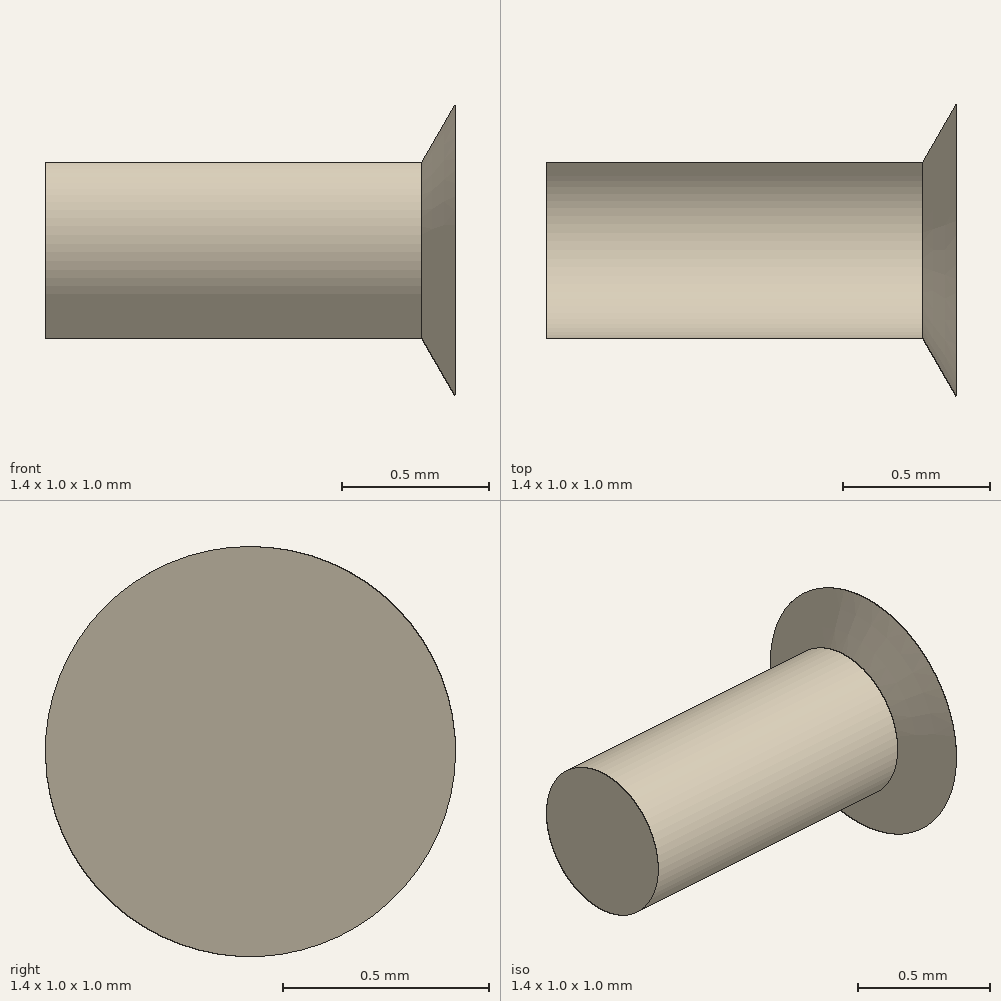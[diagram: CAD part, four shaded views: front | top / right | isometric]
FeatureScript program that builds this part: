
annotation { "Feature Type Name" : "Feature", "Feature Type Description" : "" }
export const myFeature = defineFeature(function(context is Context, id is Id, definition is map)
    precondition{}
    {
        {
            var Q0;
            Q0=qCreatedBy(makeId("Front.planeOp"),FACE);
            var sketch = newSketch(context, id + "F0", { "sketchPlane" : qUnion([Q0])});
            skLineSegment(sketch, "E0", {"start": v(0, 0) * mm, "end": v(0, 0.3) * mm});
            skLineSegment(sketch, "E1", {"start": v(0, 0.3) * mm, "end": v(1.28, 0.3) * mm});
            skLineSegment(sketch, "E2", {"start": v(1.28, 0.3) * mm, "end": v(1.4, 0.5) * mm});
            skLineSegment(sketch, "E3", {"start": v(1.4, 0.5) * mm, "end": v(1.4, 0) * mm});
            skLineSegment(sketch, "E4", {"start": v(-0.33, 0) * mm, "end": v(2.1, 0) * mm, "construction": true});
            skLineSegment(sketch, "E5", {"start": v(0, 0) * mm, "end": v(1.4, 0) * mm});
            skSolve(sketch);
        }
        {
            var Q0;
            Q0 = qSketchRegion(id + "F0", true);
            var Q1;
            Q1=sQuery(id+"F0.wireOp",EDGE,"E4");
            revolve(context, id + "F1", {"entities" : qUnion([Q0]), "axis" : qUnion([Q1]), "revolveType" : RevolveType.FULL});
        }
    });
